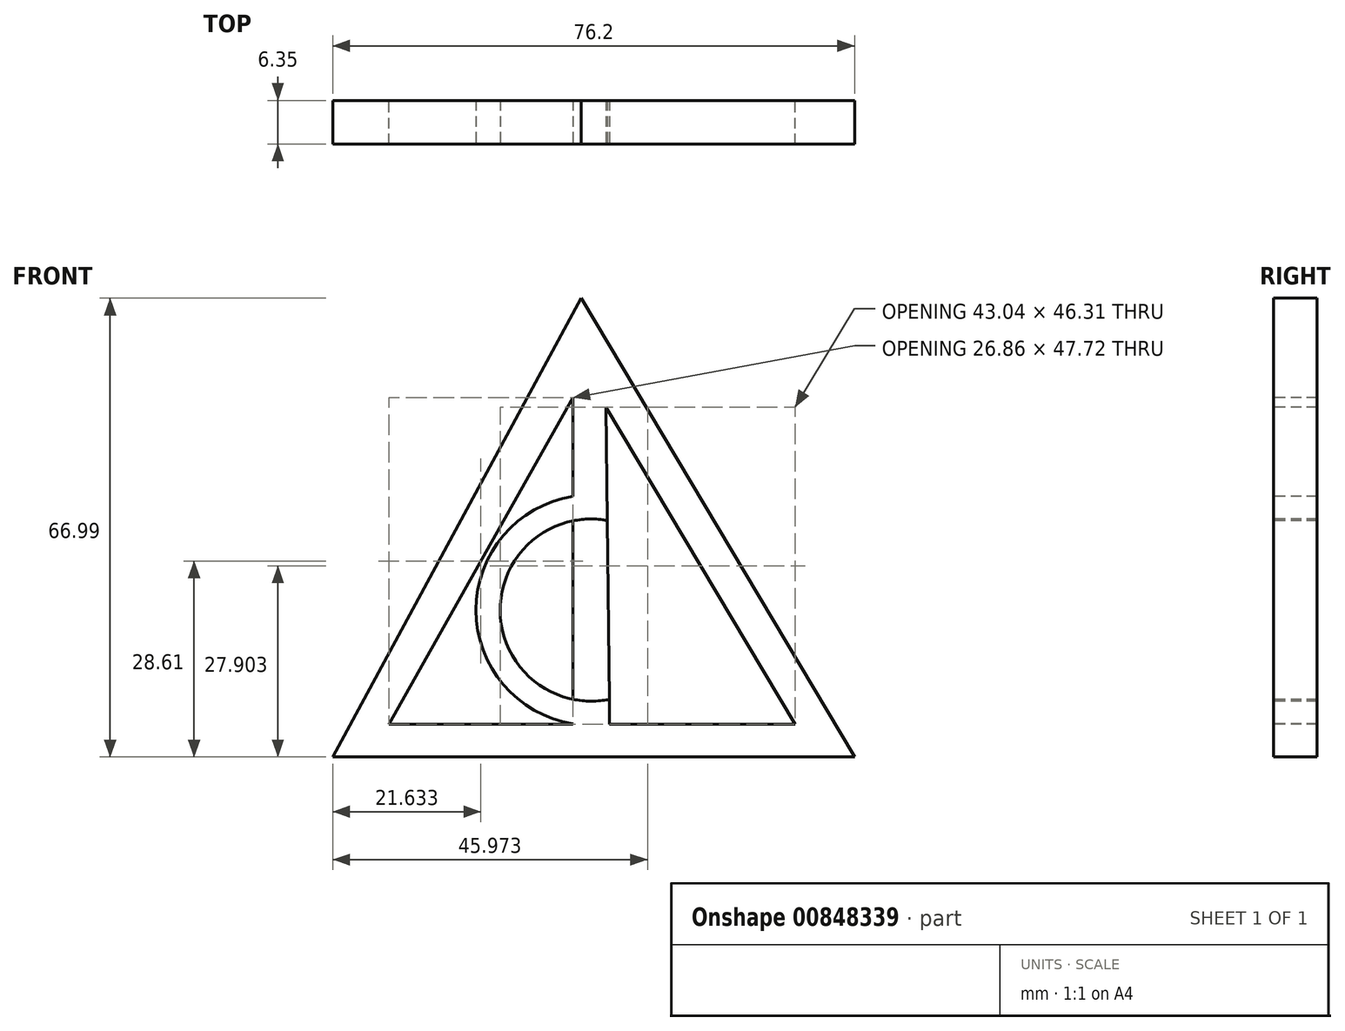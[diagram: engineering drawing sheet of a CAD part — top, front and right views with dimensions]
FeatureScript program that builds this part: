
annotation { "Feature Type Name" : "Feature", "Feature Type Description" : "" }
export const myFeature = defineFeature(function(context is Context, id is Id, definition is map)
    precondition{}
    {
        {
            var Q0;
            Q0=qCreatedBy(makeId("Front.planeOp"),FACE);
            var sketch = newSketch(context, id + "F0", { "sketchPlane" : qUnion([Q0])});
            skLineSegment(sketch, "E0", {"start": v(0, 0) * mm, "end": v(76.2, 0) * mm});
            skLineSegment(sketch, "E1", {"start": v(0, 0) * mm, "end": v(36.3, 67) * mm});
            skLineSegment(sketch, "E2", {"start": v(36.3, 67) * mm, "end": v(76.2, 0) * mm});
            skLineSegment(sketch, "E3", {"start": v(8.2, 4.75) * mm, "end": v(67.5, 4.75) * mm});
            skLineSegment(sketch, "E4", {"start": v(67.5, 4.75) * mm, "end": v(37.01, 55.93) * mm});
            skLineSegment(sketch, "E5", {"start": v(37.01, 55.93) * mm, "end": v(8.2, 4.75) * mm});
            skSolve(sketch);
        }
        {
            var Q0;
            Q0=makeQuery(id+"F0.imprint","IMPRINT",FACE,{"disambiguationData":[TD([[makeQuery(id+"F0.imprint","IMPRINT",EDGE,{"derivedFrom":sQuery(id+"F0.wireOp",EDGE,"E0")}),1.0]])]});
            extrude(context, id + "F1", {"entities" : qUnion([Q0]), "depth" : 6.35 * mm, "offsetDistance" : 25.4 * mm});
        }
        {
            var Q0;
            Q0=makeQuery(id+"F1.opExtrude","CAP_FACE",FACE,{"disambiguationData":[OSD([sQuery(id+"F0.wireOp",EDGE,"E0"),sQuery(id+"F0.wireOp",EDGE,"E1"),sQuery(id+"F0.wireOp",EDGE,"E2"),sQuery(id+"F0.wireOp",EDGE,"E3"),sQuery(id+"F0.wireOp",EDGE,"E4"),sQuery(id+"F0.wireOp",EDGE,"E5")])],"isStart":false});
            var sketch = newSketch(context, id + "F2", { "sketchPlane" : qUnion([Q0])});
            skLineSegment(sketch, "E6", {"start": v(35.06, 52.47) * mm, "end": v(35.06, 4.75) * mm});
            skLineSegment(sketch, "E7", {"start": v(35.06, 4.75) * mm, "end": v(40.44, 4.75) * mm});
            skLineSegment(sketch, "E8", {"start": v(39.92, 51.06) * mm, "end": v(40.44, 4.75) * mm});
            skLineSegment(sketch, "E9", {"start": v(35.06, 52.47) * mm, "end": v(39.92, 52.47) * mm});
            skLineSegment(sketch, "E10", {"start": v(35.06, 52.47) * mm, "end": v(37.01, 55.93) * mm});
            skLineSegment(sketch, "E11", {"start": v(37.01, 55.93) * mm, "end": v(39.92, 52.47) * mm});
            skSolve(sketch);
        }
        {
            var Q0;
            {var subQ1=sQuery(id+"F2.wireOp",EDGE,"E6");Q0=makeQuery(id+"F2.imprint","IMPRINT",FACE,{"disambiguationData":[TD([[makeQuery(id+"F2.imprint","IMPRINT",EDGE,{"derivedFrom":subQ1}),1.0]])]});}
            var Q1;
            {var subQ0=sQuery(id+"F2.wireOp",EDGE,"E10");Q1=makeQuery(id+"F2.imprint","IMPRINT",FACE,{"disambiguationData":[TD([[makeQuery(id+"F2.imprint","IMPRINT",EDGE,{"derivedFrom":subQ0}),1.0]])]});}
            extrude(context, id + "F3", {"entities" : qUnion([Q0, Q1]), "oppositeDirection" : true, "depth" : 6.35 * mm, "offsetDistance" : 25.4 * mm});
        }
        {
            var Q0;
            Q0=makeQuery(id+"F3.opExtrude","CAP_FACE",FACE,{"disambiguationData":[OSD([sQuery(id+"F0.wireOp",EDGE,"E4"),sQuery(id+"F2.wireOp",EDGE,"E6"),sQuery(id+"F2.wireOp",EDGE,"E7"),sQuery(id+"F2.wireOp",EDGE,"E8"),sQuery(id+"F2.wireOp",EDGE,"E10")])],"isStart":true});
            var sketch = newSketch(context, id + "F4", { "sketchPlane" : qUnion([Q0])});
            skCircle(sketch, "E12", {"center": v(37.75, 21.44) * mm, "radius": 16.83 * mm});
            skPoint(sketch, "E12.centerSnap0", {"position": v(37.75, 4.75) * mm});
            skSolve(sketch);
        }
        {
            var Q0;
            {var subQ0=sQuery(id+"F4.wireOp",EDGE,"E12");var subQ1=makeQuery(id+"F3.opExtrude","CAP_EDGE",EDGE,{"disambiguationData":[OSD([sQuery(id+"F2.wireOp",EDGE,"E6")])],"isStart":true});var subQ2=makeQuery(id+"F4.imprint","INTERSECT",VERTEX,{"disambiguationData":[OD(0.0)],"derivedFrom":[subQ1,subQ0]});Q0=makeQuery(id+"F4.imprint","IMPRINT",FACE,{"disambiguationData":[TD([[makeQuery(id+"F4.imprint","IMPRINT",EDGE,{"disambiguationData":[TD([[subQ2,-1.0]])],"derivedFrom":subQ0}),1.0]])]});}
            var Q1;
            {var subQ0=sQuery(id+"F4.wireOp",EDGE,"E12");var subQ1=makeQuery(id+"F3.opExtrude","CAP_EDGE",EDGE,{"disambiguationData":[OSD([sQuery(id+"F2.wireOp",EDGE,"E8")])],"isStart":true});var subQ2=makeQuery(id+"F4.imprint","INTERSECT",VERTEX,{"disambiguationData":[OD(0.0)],"derivedFrom":[subQ1,subQ0]});Q1=makeQuery(id+"F4.imprint","IMPRINT",FACE,{"disambiguationData":[TD([[makeQuery(id+"F4.imprint","IMPRINT",EDGE,{"disambiguationData":[TD([[subQ2,1.0]])],"derivedFrom":subQ0}),1.0]])]});}
            extrude(context, id + "F5", {"entities" : qUnion([Q0, Q1]), "operationType" : NewBodyOperationType.ADD, "oppositeDirection" : true, "depth" : 6.35 * mm, "offsetDistance" : 25.4 * mm});
        }
        {
            var Q0;
            {var subQ0=sQuery(id+"F4.wireOp",EDGE,"E12");var subQ1=sQuery(id+"F2.wireOp",EDGE,"E8");var subQ2=sQuery(id+"F2.wireOp",EDGE,"E6");Q0=makeQuery(id+"F5.boolean.opBoolean","MERGE",FACE,{"derivedFrom":[makeQuery(id+"F3.opExtrude","CAP_FACE",FACE,{"disambiguationData":[OSD([sQuery(id+"F0.wireOp",EDGE,"E4"),subQ2,sQuery(id+"F2.wireOp",EDGE,"E7"),subQ1,sQuery(id+"F2.wireOp",EDGE,"E10")])],"isStart":true}),makeQuery(id+"F5.opExtrude","CAP_FACE",FACE,{"disambiguationData":[OSD([subQ2,subQ0])],"isStart":true}),makeQuery(id+"F5.opExtrude","CAP_FACE",FACE,{"disambiguationData":[OSD([subQ1,subQ0])],"isStart":true})]});}
            var sketch = newSketch(context, id + "F6", { "sketchPlane" : qUnion([Q0])});
            skCircle(sketch, "E13", {"center": v(37.75, 21.44) * mm, "radius": 13.3 * mm});
            skSolve(sketch);
        }
        {
            var Q0;
            Q0=makeQuery(id+"F6.imprint","IMPRINT",FACE,{"disambiguationData":[TD([[makeQuery(id+"F6.imprint","IMPRINT",EDGE,{"derivedFrom":sQuery(id+"F6.wireOp",EDGE,"E13")}),1.0]])]});
            extrude(context, id + "F7", {"entities" : qUnion([Q0]), "operationType" : NewBodyOperationType.REMOVE, "oppositeDirection" : true, "depth" : 25.4 * mm, "offsetDistance" : 25.4 * mm});
        }
        {
            var Q0;
            {var subQ0=sQuery(id+"F4.wireOp",EDGE,"E12");var subQ1=sQuery(id+"F2.wireOp",EDGE,"E8");var subQ2=sQuery(id+"F2.wireOp",EDGE,"E6");Q0=makeQuery(id+"F5.boolean.opBoolean","MERGE",FACE,{"derivedFrom":[makeQuery(id+"F3.opExtrude","CAP_FACE",FACE,{"disambiguationData":[OSD([sQuery(id+"F0.wireOp",EDGE,"E4"),subQ2,sQuery(id+"F2.wireOp",EDGE,"E7"),subQ1,sQuery(id+"F2.wireOp",EDGE,"E10")])],"isStart":true}),makeQuery(id+"F5.opExtrude","CAP_FACE",FACE,{"disambiguationData":[OSD([subQ2,subQ0])],"isStart":true}),makeQuery(id+"F5.opExtrude","CAP_FACE",FACE,{"disambiguationData":[OSD([subQ1,subQ0])],"isStart":true})]});}
            var sketch = newSketch(context, id + "F8", { "sketchPlane" : qUnion([Q0])});
            skLineSegment(sketch, "E14", {"start": v(35.06, 38.06) * mm, "end": v(35.06, 4.83) * mm});
            skLineSegment(sketch, "E15", {"start": v(40.44, 4.75) * mm, "end": v(40.06, 38.11) * mm});
            skSolve(sketch);
        }
        {
            var Q0;
            {var subQ0=sQuery(id+"F8.wireOp",EDGE,"E14");var subQ1=makeQuery(id+"F7.boolean.opBoolean","COPY",EDGE,{"derivedFrom":makeQuery(id+"F7.opExtrude","CAP_EDGE",EDGE,{"disambiguationData":[OSD([sQuery(id+"F6.wireOp",EDGE,"E13")])],"isStart":true})});var subQ2=makeQuery(id+"F8.imprint","INTERSECT",VERTEX,{"disambiguationData":[OD(0.0)],"derivedFrom":[subQ1,subQ0]});Q0=makeQuery(id+"F8.imprint","IMPRINT",FACE,{"disambiguationData":[TD([[makeQuery(id+"F8.imprint","IMPRINT",EDGE,{"disambiguationData":[TD([[subQ2,-1.0]])],"derivedFrom":subQ0}),1.0]])]});}
            extrude(context, id + "F9", {"entities" : qUnion([Q0]), "oppositeDirection" : true, "depth" : 6.35 * mm, "offsetDistance" : 25.4 * mm});
        }
    });
